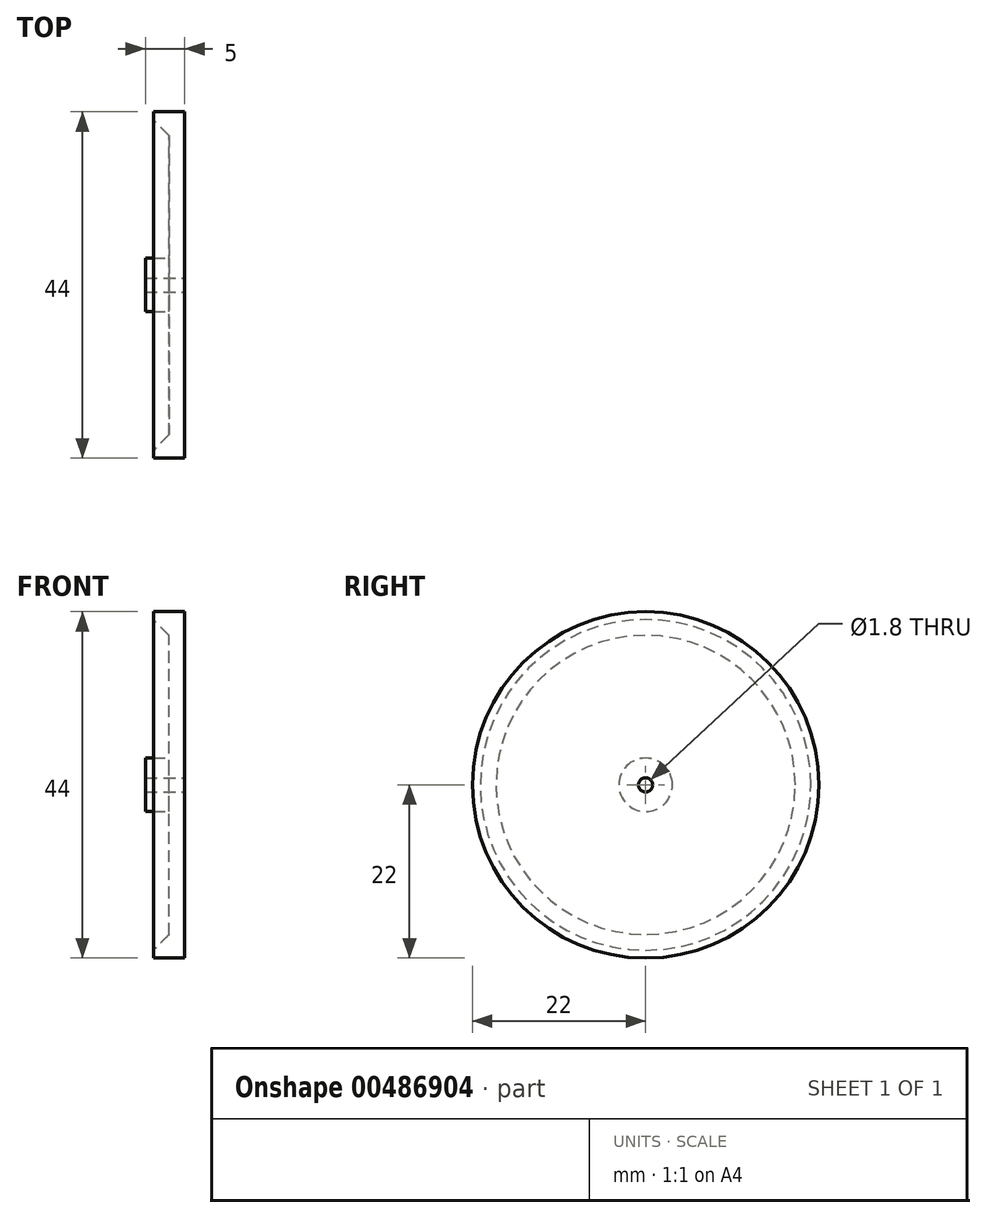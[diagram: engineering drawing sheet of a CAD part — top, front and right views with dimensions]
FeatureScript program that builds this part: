
annotation { "Feature Type Name" : "Feature", "Feature Type Description" : "" }
export const myFeature = defineFeature(function(context is Context, id is Id, definition is map)
    precondition{}
    {
        {
            var Q0;
            Q0=qCreatedBy(makeId("Front.planeOp"),FACE);
            var sketch = newSketch(context, id + "F0", { "sketchPlane" : qUnion([Q0])});
            skLineSegment(sketch, "E0.top", {"start": v(-1.05, 22) * mm, "end": v(-3.05, 22) * mm});
            skLineSegment(sketch, "E0.left", {"start": v(-1.05, 0.9) * mm, "end": v(-1.05, 22) * mm});
            skLineSegment(sketch, "E0.right", {"start": v(-3.05, 3.4) * mm, "end": v(-3.05, 19) * mm});
            skLineSegment(sketch, "E1.bottom", {"start": v(-3.05, 22) * mm, "end": v(-5.05, 22) * mm});
            skLineSegment(sketch, "E1.right", {"start": v(-5.05, 22) * mm, "end": v(-5.05, 21) * mm});
            skLineSegment(sketch, "E2.top", {"start": v(-3.05, 0.9) * mm, "end": v(-5.83, 0.9) * mm});
            skLineSegment(sketch, "E3", {"start": v(-5.05, 21) * mm, "end": v(-3.05, 19) * mm});
            skLineSegment(sketch, "E4.bottom", {"start": v(-1.05, 0.9) * mm, "end": v(-6.05, 0.9) * mm});
            skLineSegment(sketch, "E4.top", {"start": v(-3.05, 3.4) * mm, "end": v(-6.05, 3.4) * mm});
            skLineSegment(sketch, "E4.left", {"start": v(-1.05, 0.9) * mm, "end": v(-1.05, 3.4) * mm});
            skLineSegment(sketch, "E4.right", {"start": v(-6.05, 0.9) * mm, "end": v(-6.05, 3.4) * mm});
            skLineSegment(sketch, "E5", {"start": v(0.85, 0) * mm, "end": v(-23.16, 0) * mm, "construction": true});
            skSolve(sketch);
        }
        {
            var Q0;
            Q0=makeQuery(id+"F0.imprint","IMPRINT",FACE,{"disambiguationData":[TD([[makeQuery(id+"F0.imprint","IMPRINT",EDGE,{"derivedFrom":sQuery(id+"F0.wireOp",EDGE,"E0.top")}),1.0]])]});
            var Q1;
            Q1=sQuery(id+"F0.wireOp",EDGE,"E5");
            revolve(context, id + "F1", {"entities" : qUnion([Q0]), "axis" : qUnion([Q1]), "revolveType" : RevolveType.FULL});
        }
    });
